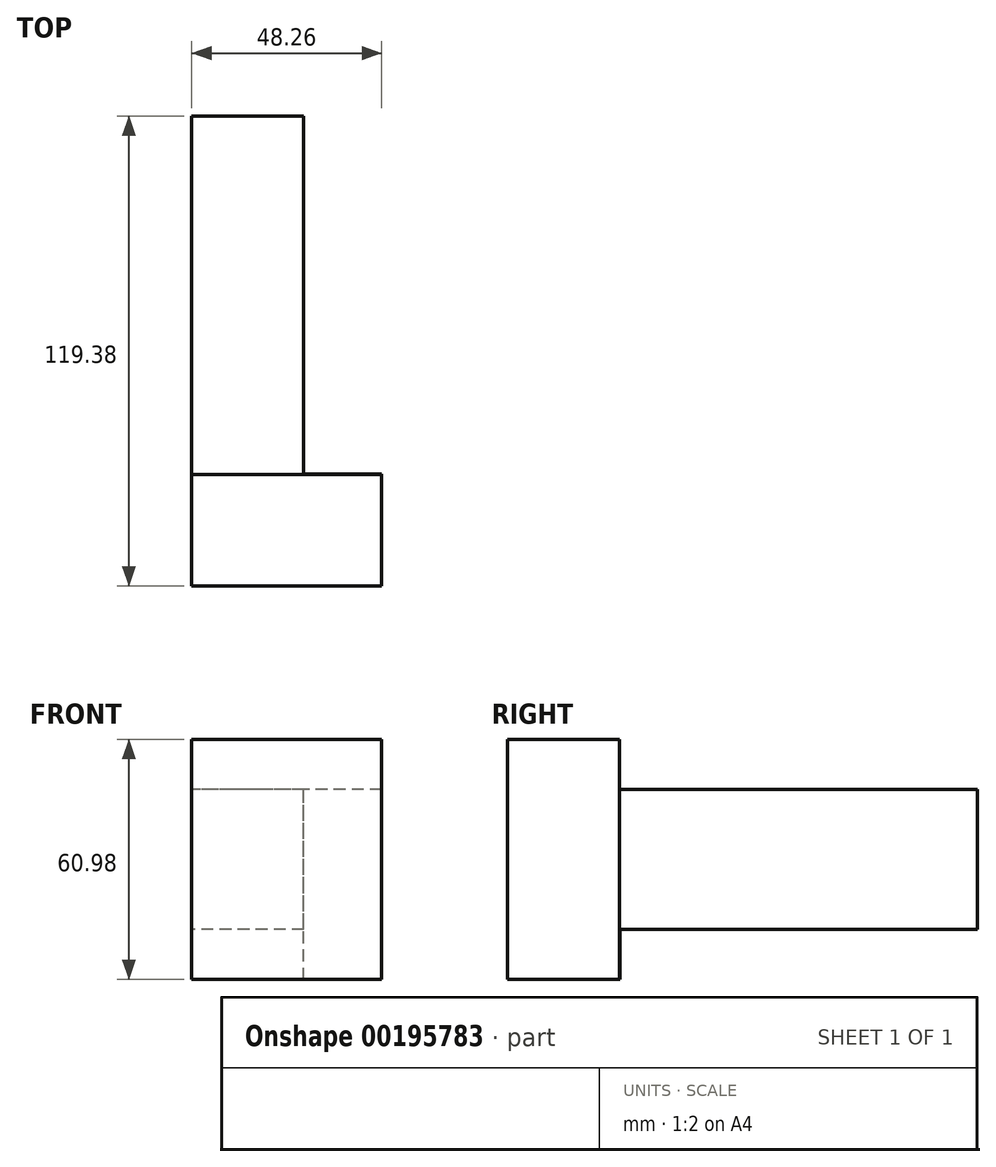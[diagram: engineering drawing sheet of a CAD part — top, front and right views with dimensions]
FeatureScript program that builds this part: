
annotation { "Feature Type Name" : "Feature", "Feature Type Description" : "" }
export const myFeature = defineFeature(function(context is Context, id is Id, definition is map)
    precondition{}
    {
        {
            var Q0;
            Q0=qCreatedBy(makeId("Right.planeOp"),FACE);
            var sketch = newSketch(context, id + "F0", { "sketchPlane" : qUnion([Q0])});
            skLineSegment(sketch, "E0.bottom", {"start": v(0, 3.58) * mm, "end": v(-119.38, 3.58) * mm});
            skLineSegment(sketch, "E0.top", {"start": v(0, 39.16) * mm, "end": v(-119.38, 39.16) * mm});
            skLineSegment(sketch, "E0.left", {"start": v(0, 3.58) * mm, "end": v(0, 39.16) * mm});
            skLineSegment(sketch, "E0.right", {"start": v(-119.38, 3.58) * mm, "end": v(-119.38, 39.16) * mm});
            skSolve(sketch);
        }
        {
            var Q0;
            Q0=makeQuery(id+"F0.imprint","IMPRINT",FACE,{"disambiguationData":[TD([[makeQuery(id+"F0.imprint","IMPRINT",EDGE,{"derivedFrom":sQuery(id+"F0.wireOp",EDGE,"E0.bottom")}),-1.0]])]});
            extrude(context, id + "F1", {"entities" : qUnion([Q0]), "depth" : 28.45 * mm});
        }
        {
            var Q0;
            Q0=makeQuery(id+"F1.opExtrude","CAP_FACE",FACE,{"disambiguationData":[OSD([sQuery(id+"F0.wireOp",EDGE,"E0.bottom"),sQuery(id+"F0.wireOp",EDGE,"E0.top"),sQuery(id+"F0.wireOp",EDGE,"E0.left"),sQuery(id+"F0.wireOp",EDGE,"E0.right")])],"isStart":false});
            var sketch = newSketch(context, id + "F2", { "sketchPlane" : qUnion([Q0])});
            skLineSegment(sketch, "E1.bottom", {"start": v(-119.38, 3.58) * mm, "end": v(-90.93, 3.58) * mm});
            skLineSegment(sketch, "E1.top", {"start": v(-119.38, 39.16) * mm, "end": v(-90.93, 39.16) * mm});
            skLineSegment(sketch, "E1.left", {"start": v(-119.38, 3.58) * mm, "end": v(-119.38, 39.16) * mm});
            skLineSegment(sketch, "E1.right", {"start": v(-90.93, 3.58) * mm, "end": v(-90.93, 39.16) * mm});
            skSolve(sketch);
        }
        {
            var Q0;
            Q0=makeQuery(id+"F1.opExtrude","SWEPT_FACE",FACE,{"disambiguationData":[OSD([sQuery(id+"F0.wireOp",EDGE,"E0.bottom")])]});
            var sketch = newSketch(context, id + "F3", { "sketchPlane" : qUnion([Q0])});
            skLineSegment(sketch, "E2", {"start": v(28.45, 90.92) * mm, "end": v(0, 90.92) * mm});
            skSolve(sketch);
        }
        {
            var Q0;
            Q0=makeQuery(id+"F1.opExtrude","SWEPT_FACE",FACE,{"disambiguationData":[OSD([sQuery(id+"F0.wireOp",EDGE,"E0.top")])]});
            var sketch = newSketch(context, id + "F4", { "sketchPlane" : qUnion([Q0])});
            skLineSegment(sketch, "E3", {"start": v(28.45, -91.04) * mm, "end": v(0, -91.04) * mm});
            skSolve(sketch);
        }
        {
            var Q0;
            Q0=makeQuery(id+"F2.imprint","IMPRINT",FACE,{"disambiguationData":[TD([[makeQuery(id+"F2.imprint","IMPRINT",EDGE,{"derivedFrom":sQuery(id+"F2.wireOp",EDGE,"E1.bottom")}),-1.0]])]});
            extrude(context, id + "F5", {"entities" : qUnion([Q0]), "operationType" : NewBodyOperationType.ADD, "depth" : 19.8 * mm});
        }
        {
            var Q0;
            {var subQ0=sQuery(id+"F3.wireOp",EDGE,"E2");Q0=makeQuery(id+"F3.imprint","IMPRINT",FACE,{"disambiguationData":[TD([[makeQuery(id+"F3.imprint","IMPRINT",EDGE,{"derivedFrom":subQ0}),-1.0]])]});}
            extrude(context, id + "F6", {"entities" : qUnion([Q0]), "operationType" : NewBodyOperationType.ADD, "depth" : 12.7 * mm});
        }
        {
            var Q0;
            {var subQ1=sQuery(id+"F0.wireOp",EDGE,"E0.right");var subQ3=sQuery(id+"F2.wireOp",EDGE,"E1.bottom");var subQ4=sQuery(id+"F0.wireOp",EDGE,"E0.bottom");Q0=makeQuery(id+"F6.boolean.opBoolean","SPLIT",FACE,{"disambiguationData":[TD([makeQuery(id+"F1.opExtrude","SWEPT_FACE",FACE,{"disambiguationData":[OSD([subQ1])]})])],"derivedFrom":makeQuery(id+"F5.boolean.opBoolean","MERGE",FACE,{"derivedFrom":[makeQuery(id+"F1.opExtrude","SWEPT_FACE",FACE,{"disambiguationData":[OSD([subQ4])]}),makeQuery(id+"F5.opExtrude","SWEPT_FACE",FACE,{"disambiguationData":[OSD([subQ3])]})]})});}
            extrude(context, id + "F7", {"entities" : qUnion([Q0]), "operationType" : NewBodyOperationType.ADD, "depth" : 12.7 * mm});
        }
        {
            var Q0;
            {var subQ0=sQuery(id+"F4.wireOp",EDGE,"E3");Q0=makeQuery(id+"F4.imprint","IMPRINT",FACE,{"disambiguationData":[TD([[makeQuery(id+"F4.imprint","IMPRINT",EDGE,{"derivedFrom":subQ0}),1.0]])]});}
            extrude(context, id + "F8", {"entities" : qUnion([Q0]), "operationType" : NewBodyOperationType.ADD, "depth" : 12.7 * mm});
        }
        {
            var Q0;
            {var subQ0=sQuery(id+"F0.wireOp",EDGE,"E0.top");var subQ1=makeQuery(id+"F1.opExtrude","CAP_EDGE",EDGE,{"disambiguationData":[OSD([subQ0])],"isStart":false});Q0=makeQuery(id+"F8.opExtrude","SWEPT_FACE",FACE,{"disambiguationData":[OSD([subQ0]),TDD([makeQuery(id+"F4.imprint","IMPRINT",EDGE,{"disambiguationData":[TD([[makeQuery(id+"F4.imprint","INTERSECT",VERTEX,{"derivedFrom":[subQ1,sQuery(id+"F4.wireOp",EDGE,"E3")]}),-1.0]])],"derivedFrom":subQ1})])]});}
            extrude(context, id + "F9", {"entities" : qUnion([Q0]), "operationType" : NewBodyOperationType.ADD, "depth" : 19.8 * mm});
        }
        {
            var Q0;
            {var subQ0=sQuery(id+"F0.wireOp",EDGE,"E0.bottom");var subQ1=makeQuery(id+"F1.opExtrude","CAP_EDGE",EDGE,{"disambiguationData":[OSD([subQ0])],"isStart":false});var subQ2=sQuery(id+"F0.wireOp",EDGE,"E0.right");Q0=makeQuery(id+"F6.boolean.opBoolean","MERGE",FACE,{"derivedFrom":[makeQuery(id+"F1.opExtrude","CAP_FACE",FACE,{"disambiguationData":[OSD([subQ0,sQuery(id+"F0.wireOp",EDGE,"E0.top"),sQuery(id+"F0.wireOp",EDGE,"E0.left"),subQ2])],"isStart":false}),makeQuery(id+"F6.opExtrude","SWEPT_FACE",FACE,{"disambiguationData":[OSD([subQ0]),TDD([makeQuery(id+"F3.imprint","IMPRINT",EDGE,{"disambiguationData":[TD([[makeQuery(id+"F3.imprint","INTERSECT",VERTEX,{"derivedFrom":[subQ1,sQuery(id+"F3.wireOp",EDGE,"E2")]}),-1.0]])],"derivedFrom":subQ1})])]})]});}
            var sketch = newSketch(context, id + "F10", { "sketchPlane" : qUnion([Q0])});
            skLineSegment(sketch, "E4", {"start": v(-29.77, 39.16) * mm, "end": v(0, 21.37) * mm});
            skLineSegment(sketch, "E5", {"start": v(0, 21.37) * mm, "end": v(-29.77, 3.58) * mm});
            skSolve(sketch);
        }
        {
            var Q0;
            {var subQ0=sQuery(id+"F10.wireOp",EDGE,"E4");Q0=makeQuery(id+"F10.imprint","IMPRINT",FACE,{"disambiguationData":[TD([[makeQuery(id+"F10.imprint","IMPRINT",EDGE,{"derivedFrom":subQ0}),1.0]])]});}
            extrude(context, id + "F11", {"entities" : qUnion([Q0]), "operationType" : NewBodyOperationType.ADD, "oppositeDirection" : true, "depth" : 28.2 * mm});
        }
    });
